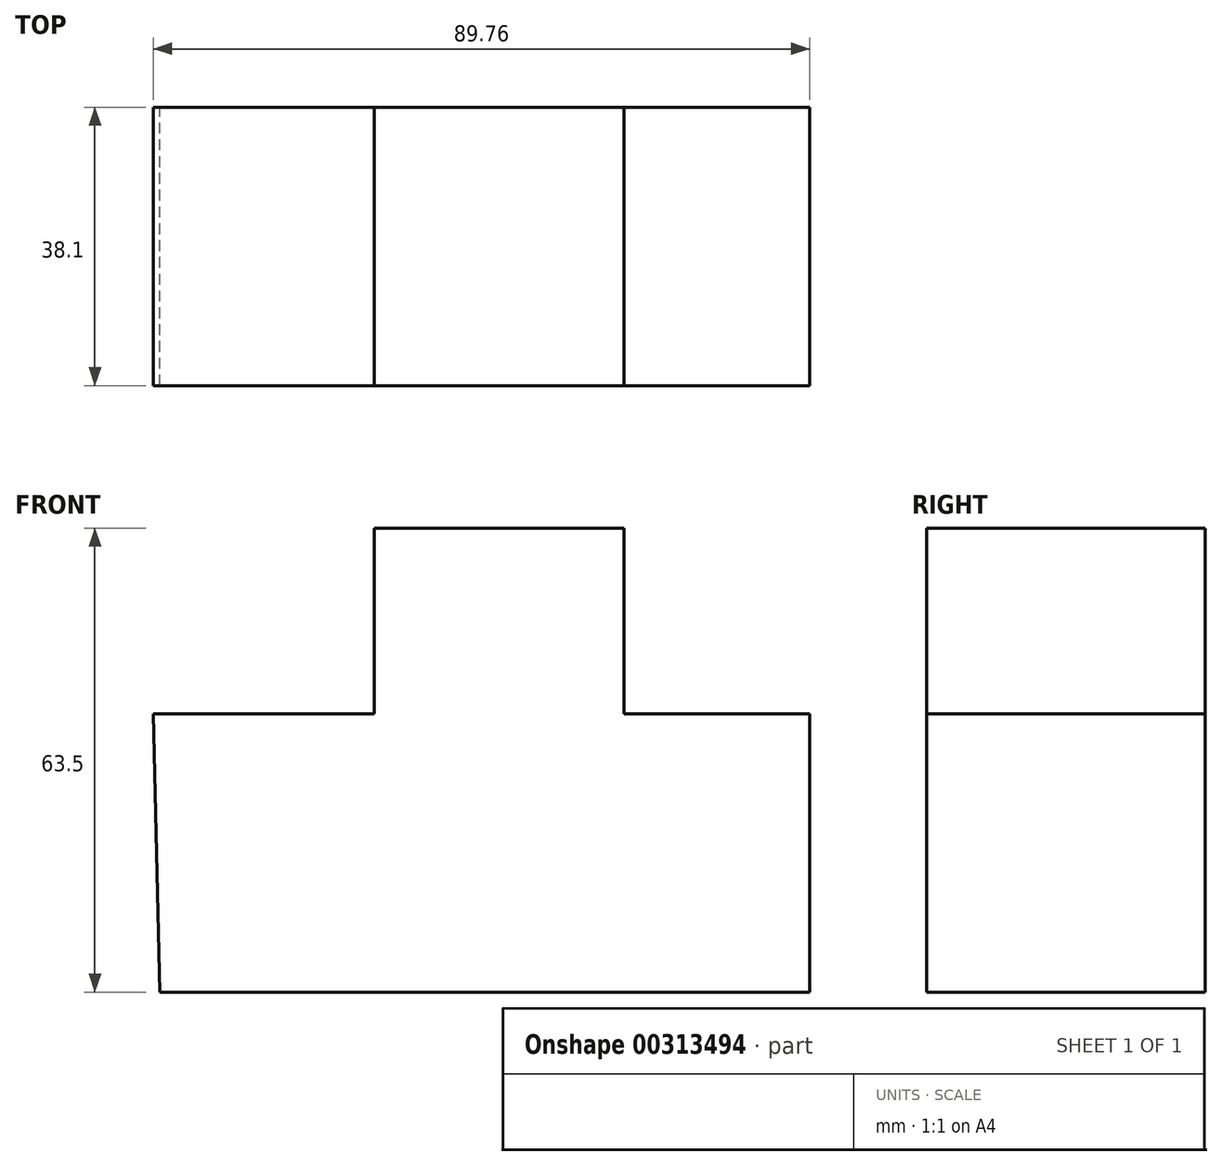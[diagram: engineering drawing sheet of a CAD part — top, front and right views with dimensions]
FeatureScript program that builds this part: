
annotation { "Feature Type Name" : "Feature", "Feature Type Description" : "" }
export const myFeature = defineFeature(function(context is Context, id is Id, definition is map)
    precondition{}
    {
        {
            var Q0;
            Q0=qCreatedBy(makeId("Front.planeOp"),FACE);
            var sketch = newSketch(context, id + "F0", { "sketchPlane" : qUnion([Q0])});
            skLineSegment(sketch, "E0", {"start": v(-46.13, -25.4) * mm, "end": v(42.77, -25.4) * mm});
            skLineSegment(sketch, "E1", {"start": v(42.77, -25.4) * mm, "end": v(42.77, 12.7) * mm});
            skLineSegment(sketch, "E2", {"start": v(42.77, 12.7) * mm, "end": v(17.37, 12.7) * mm});
            skLineSegment(sketch, "E3", {"start": v(17.37, 12.7) * mm, "end": v(17.37, 38.1) * mm});
            skLineSegment(sketch, "E4", {"start": v(17.37, 38.1) * mm, "end": v(-16.78, 38.1) * mm});
            skLineSegment(sketch, "E5", {"start": v(-16.78, 38.1) * mm, "end": v(-16.78, 12.7) * mm});
            skLineSegment(sketch, "E6", {"start": v(-16.78, 12.7) * mm, "end": v(-46.99, 12.7) * mm});
            skLineSegment(sketch, "E7", {"start": v(-46.99, 12.7) * mm, "end": v(-46.13, -25.4) * mm});
            skSolve(sketch);
        }
        {
            var Q0;
            Q0=makeQuery(id+"F0.imprint","IMPRINT",FACE,{"disambiguationData":[TD([[makeQuery(id+"F0.imprint","IMPRINT",EDGE,{"derivedFrom":sQuery(id+"F0.wireOp",EDGE,"E0")}),1.0]])]});
            extrude(context, id + "F1", {"entities" : qUnion([Q0]), "depth" : 38.1 * mm});
        }
    });
